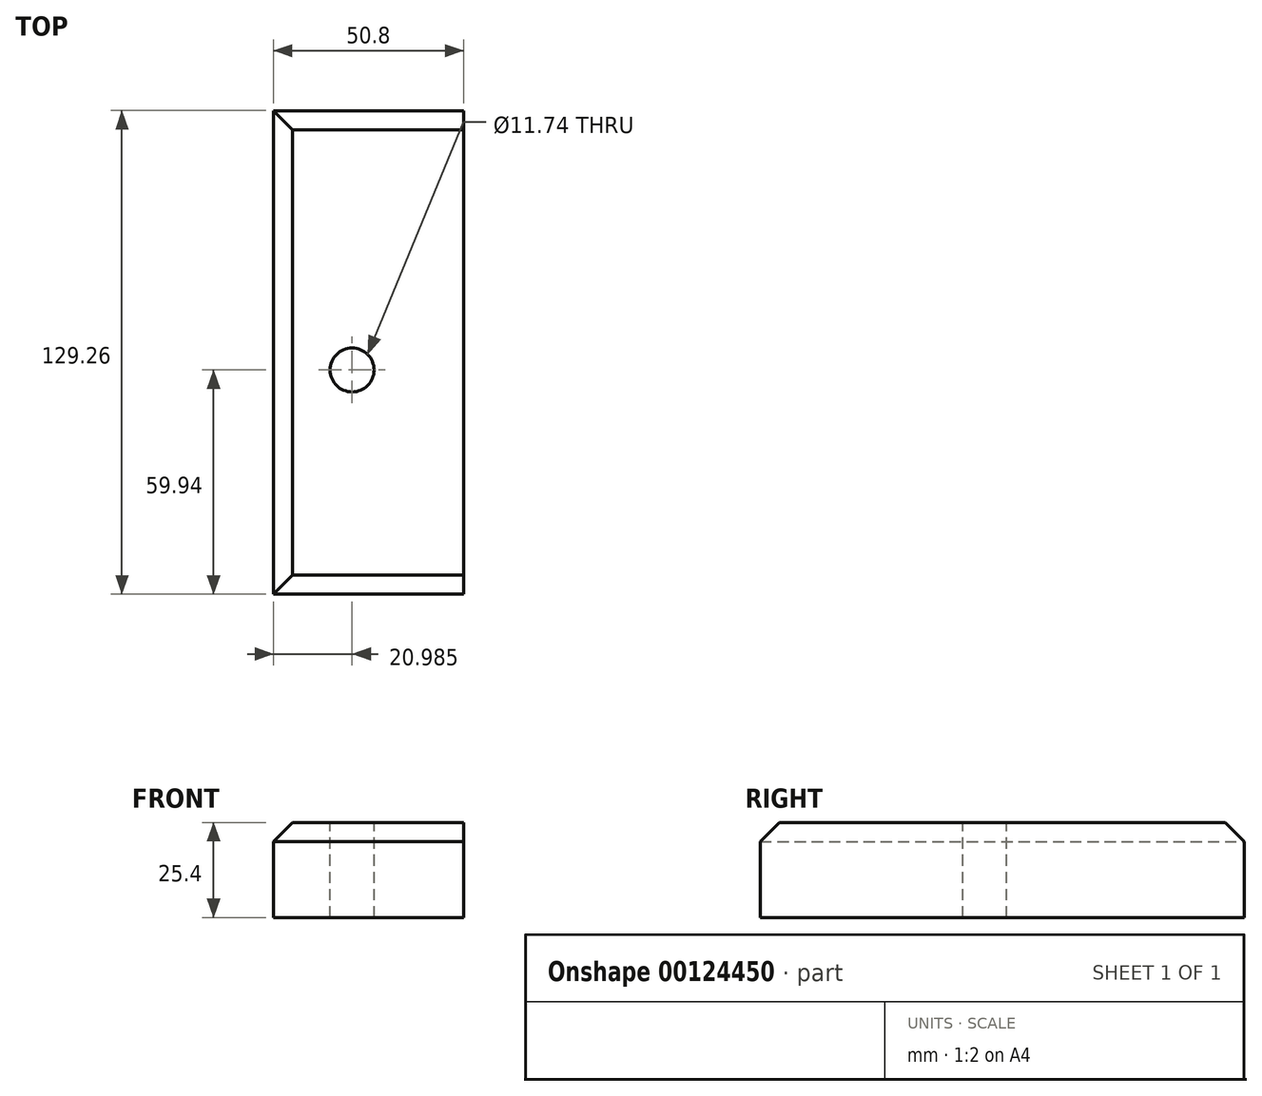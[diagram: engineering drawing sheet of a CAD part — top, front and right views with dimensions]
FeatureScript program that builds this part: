
annotation { "Feature Type Name" : "Feature", "Feature Type Description" : "" }
export const myFeature = defineFeature(function(context is Context, id is Id, definition is map)
    precondition{}
    {
        {
            var Q0;
            Q0=qCreatedBy(makeId("Top.planeOp"),FACE);
            var sketch = newSketch(context, id + "F0", { "sketchPlane" : qUnion([Q0])});
            skLineSegment(sketch, "E0.bottom", {"start": v(-57.1, 69.32) * mm, "end": v(-6.3, 69.32) * mm});
            skLineSegment(sketch, "E0.top", {"start": v(-57.1, -59.94) * mm, "end": v(-6.3, -59.94) * mm});
            skLineSegment(sketch, "E0.left", {"start": v(-57.1, 69.32) * mm, "end": v(-57.1, -59.94) * mm});
            skLineSegment(sketch, "E0.right", {"start": v(-6.3, 69.32) * mm, "end": v(-6.3, -59.94) * mm});
            skSolve(sketch);
        }
        {
            var Q0;
            Q0 = qSketchRegion(id + "F0", true);
            var Q1;
            Q1=makeQuery(id+"F0.imprint","IMPRINT",FACE,{"disambiguationData":[TD([[makeQuery(id+"F0.imprint","IMPRINT",EDGE,{"derivedFrom":sQuery(id+"F0.wireOp",EDGE,"E0.bottom")}),-1.0]])]});
            extrude(context, id + "F1", {"entities" : qUnion([Q0, Q1]), "oppositeDirection" : true, "depth" : 25.4 * mm});
        }
        {
            var Q0;
            Q0=makeQuery(id+"F1.opExtrude","CAP_EDGE",EDGE,{"disambiguationData":[OSD([sQuery(id+"F0.wireOp",EDGE,"E0.left")])],"isStart":true});
            var Q1;
            Q1=makeQuery(id+"F1.opExtrude","CAP_EDGE",EDGE,{"disambiguationData":[OSD([sQuery(id+"F0.wireOp",EDGE,"E0.top")])],"isStart":true});
            var Q2;
            Q2=makeQuery(id+"F1.opExtrude","CAP_EDGE",EDGE,{"disambiguationData":[OSD([sQuery(id+"F0.wireOp",EDGE,"E0.bottom")])],"isStart":true});
            chamfer(context, id + "F2", {"entities" : qUnion([Q0, Q1, Q2]), "width" : 5.08 * mm, "tangentPropagation" : true});
        }
        {
            var Q0;
            Q0=makeQuery(id+"F1.opExtrude","CAP_FACE",FACE,{"disambiguationData":[OSD([sQuery(id+"F0.wireOp",EDGE,"E0.bottom"),sQuery(id+"F0.wireOp",EDGE,"E0.top"),sQuery(id+"F0.wireOp",EDGE,"E0.left"),sQuery(id+"F0.wireOp",EDGE,"E0.right")])],"isStart":true});
            var sketch = newSketch(context, id + "F3", { "sketchPlane" : qUnion([Q0])});
            skCircle(sketch, "E1", {"center": v(-36.1, 0) * mm, "radius": 5.87 * mm});
            skSolve(sketch);
        }
        {
            var Q0;
            Q0=makeQuery(id+"F3.imprint","IMPRINT",FACE,{"disambiguationData":[TD([[makeQuery(id+"F3.imprint","IMPRINT",EDGE,{"derivedFrom":sQuery(id+"F3.wireOp",EDGE,"E1")}),1.0]])]});
            extrude(context, id + "F4", {"entities" : qUnion([Q0]), "operationType" : NewBodyOperationType.REMOVE, "oppositeDirection" : true, "depth" : 25.4 * mm});
        }
    });
